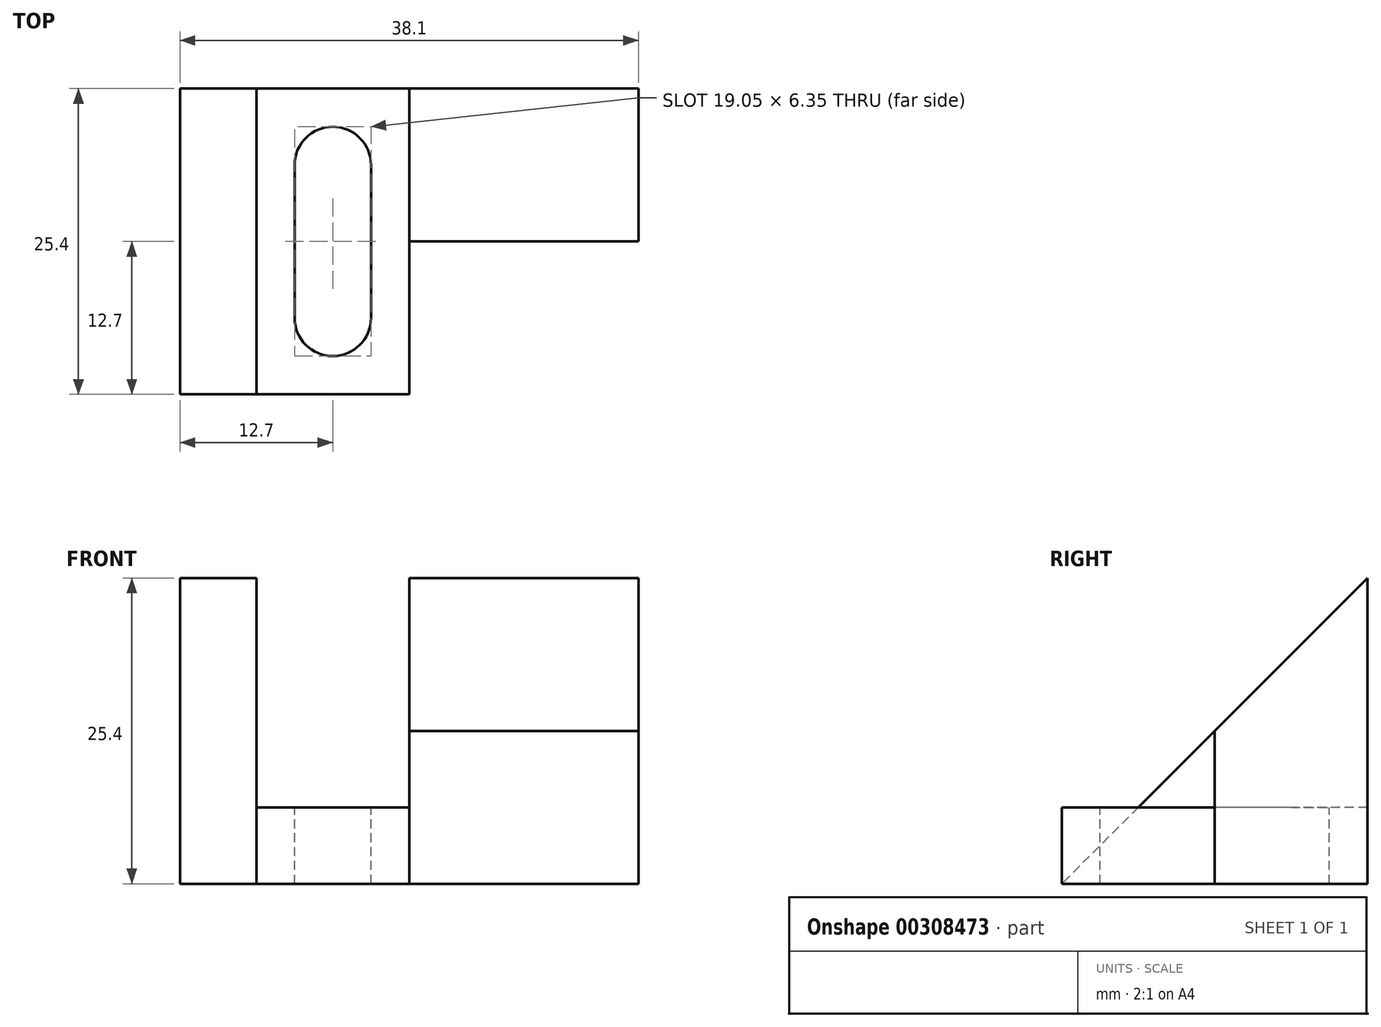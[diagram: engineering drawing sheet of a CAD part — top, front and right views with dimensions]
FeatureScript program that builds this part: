
annotation { "Feature Type Name" : "Feature", "Feature Type Description" : "" }
export const myFeature = defineFeature(function(context is Context, id is Id, definition is map)
    precondition{}
    {
        {
            var Q0;
            Q0=qCreatedBy(makeId("Right.planeOp"),FACE);
            var sketch = newSketch(context, id + "F0", { "sketchPlane" : qUnion([Q0])});
            skLineSegment(sketch, "E0", {"start": v(0, 25.4) * mm, "end": v(0, 0) * mm});
            skLineSegment(sketch, "E1", {"start": v(0, 0) * mm, "end": v(-25.4, 0) * mm});
            skLineSegment(sketch, "E2", {"start": v(-25.4, 0) * mm, "end": v(-25.4, 6.35) * mm});
            skLineSegment(sketch, "E3", {"start": v(-25.4, 6.35) * mm, "end": v(-19.05, 6.35) * mm});
            skLineSegment(sketch, "E4", {"start": v(-19.05, 6.35) * mm, "end": v(0, 25.4) * mm});
            skSolve(sketch);
        }
        {
            var Q0;
            Q0 = qSketchRegion(id + "F0", true);
            extrude(context, id + "F1", {"entities" : qUnion([Q0]), "depth" : 38.1 * mm});
        }
        {
            var Q0;
            Q0=makeQuery(id+"F1.opExtrude","CAP_FACE",FACE,{"disambiguationData":[OSD([sQuery(id+"F0.wireOp",EDGE,"E0"),sQuery(id+"F0.wireOp",EDGE,"E1"),sQuery(id+"F0.wireOp",EDGE,"E2"),sQuery(id+"F0.wireOp",EDGE,"E3"),sQuery(id+"F0.wireOp",EDGE,"E4")])],"isStart":false});
            var sketch = newSketch(context, id + "F2", { "sketchPlane" : qUnion([Q0])});
            skLineSegment(sketch, "E5", {"start": v(-25.4, 0) * mm, "end": v(-12.7, 0) * mm});
            skLineSegment(sketch, "E6", {"start": v(-12.7, 0) * mm, "end": v(-12.7, 12.7) * mm});
            skLineSegment(sketch, "E7", {"start": v(-12.7, 12.7) * mm, "end": v(-19.05, 6.35) * mm});
            skLineSegment(sketch, "E8", {"start": v(-19.05, 6.35) * mm, "end": v(-25.4, 6.35) * mm});
            skLineSegment(sketch, "E9", {"start": v(-25.4, 6.35) * mm, "end": v(-25.4, 0) * mm});
            skSolve(sketch);
        }
        {
            var Q0;
            Q0=makeQuery(id+"F1.opExtrude","CAP_FACE",FACE,{"disambiguationData":[OSD([sQuery(id+"F0.wireOp",EDGE,"E0"),sQuery(id+"F0.wireOp",EDGE,"E1"),sQuery(id+"F0.wireOp",EDGE,"E2"),sQuery(id+"F0.wireOp",EDGE,"E3"),sQuery(id+"F0.wireOp",EDGE,"E4")])],"isStart":true});
            var sketch = newSketch(context, id + "F3", { "sketchPlane" : qUnion([Q0])});
            skLineSegment(sketch, "E10", {"start": v(19.05, 6.35) * mm, "end": v(25.4, 0) * mm});
            skSolve(sketch);
        }
        {
            var Q0;
            Q0 = qSketchRegion(id + "F3", true);
            var Q1;
            Q1=makeQuery(id+"F3.imprint","IMPRINT",FACE,{"disambiguationData":[TD([[makeQuery(id+"F3.imprint","IMPRINT",EDGE,{"derivedFrom":sQuery(id+"F3.wireOp",EDGE,"E10")}),1.0]])]});
            extrude(context, id + "F4", {"entities" : qUnion([Q0, Q1]), "operationType" : NewBodyOperationType.REMOVE, "oppositeDirection" : true, "depth" : 6.35 * mm});
        }
        {
            var Q0;
            Q0 = qSketchRegion(id + "F2", true);
            extrude(context, id + "F5", {"entities" : qUnion([Q0]), "operationType" : NewBodyOperationType.REMOVE, "oppositeDirection" : true, "depth" : 19.05 * mm});
        }
        {
            var Q0;
            Q0=makeQuery(id+"F1.opExtrude","SWEPT_FACE",FACE,{"disambiguationData":[OSD([sQuery(id+"F0.wireOp",EDGE,"E2")])]});
            var sketch = newSketch(context, id + "F6", { "sketchPlane" : qUnion([Q0])});
            skLineSegment(sketch, "E11", {"start": v(19.05, 6.35) * mm, "end": v(19.05, 25.9) * mm});
            skLineSegment(sketch, "E12", {"start": v(19.05, 25.9) * mm, "end": v(6.35, 25.9) * mm});
            skLineSegment(sketch, "E13", {"start": v(6.35, 25.9) * mm, "end": v(6.35, 6.35) * mm});
            skLineSegment(sketch, "E14", {"start": v(6.35, 6.35) * mm, "end": v(19.05, 6.35) * mm});
            skSolve(sketch);
        }
        {
            var Q0;
            Q0 = qSketchRegion(id + "F6", true);
            extrude(context, id + "F7", {"entities" : qUnion([Q0]), "operationType" : NewBodyOperationType.REMOVE, "endBound" : BoundingType.THROUGH_ALL, "oppositeDirection" : true, "depth" : 25.4 * mm});
        }
        {
            var Q0;
            Q0=makeQuery(id+"F7.boolean.opBoolean","MERGE",FACE,{"derivedFrom":[makeQuery(id+"F1.opExtrude","SWEPT_FACE",FACE,{"disambiguationData":[OSD([sQuery(id+"F0.wireOp",EDGE,"E3")])]}),makeQuery(id+"F7.opExtrude","SWEPT_FACE",FACE,{"disambiguationData":[OSD([sQuery(id+"F6.wireOp",EDGE,"E14")])]})]});
            var sketch = newSketch(context, id + "F8", { "sketchPlane" : qUnion([Q0])});
            skLineSegment(sketch, "E15", {"start": v(9.53, -6.35) * mm, "end": v(9.53, -19.05) * mm});
            skLineSegment(sketch, "E16", {"start": v(15.88, -6.35) * mm, "end": v(15.88, -19.05) * mm});
            skArc(sketch, "E17", {"start": v(15.88, -6.35) * mm, "mid": v(12.7, -3.18) * mm, "end": v(9.53, -6.35) * mm});
            skArc(sketch, "E18", {"start": v(9.53, -19.05) * mm, "mid": v(12.7, -22.22) * mm, "end": v(15.88, -19.05) * mm});
            skSolve(sketch);
        }
        {
            var Q0;
            Q0 = qSketchRegion(id + "F8", true);
            extrude(context, id + "F9", {"entities" : qUnion([Q0]), "operationType" : NewBodyOperationType.REMOVE, "endBound" : BoundingType.THROUGH_ALL, "oppositeDirection" : true, "depth" : 25.4 * mm});
        }
    });
